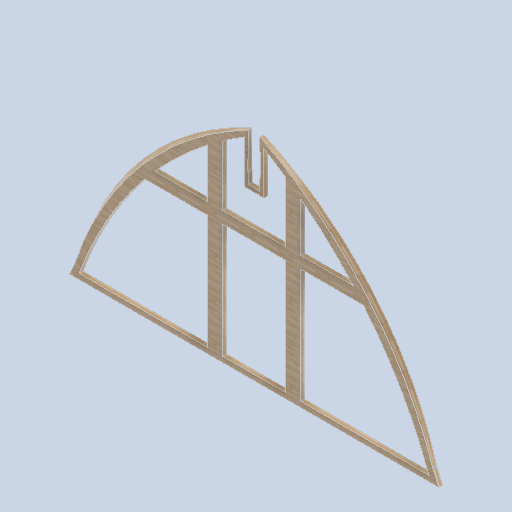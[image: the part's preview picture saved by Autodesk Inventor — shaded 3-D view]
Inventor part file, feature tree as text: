
AUTODESK INVENTOR PART (.ipt)
format: ipt  version: 2024.2 (Build 282272000, 272)  size: 438,784 bytes
history: native  units: mm
features: sketch x4, plane x2, extrude x2, loft x1
ambient origin geometry x8: Origin, YZ Plane, XZ Plane, XY Plane, X Axis, Y Axis, Z Axis, Center Point
bodies: Solid1 (feature_tree)
feature tree (9):
  sketch  "Sketch1"  dims[d2=0.0mm d3=-100.0mm d5=7.0mm]
  plane  "Work Plane2"
  loft  "Loft1"
  extrude  "Extrusion1"  TaperAngle=0.0deg  [1 undecoded]
  extrude  "Extrusion2"  Depth=10000.0mm
  plane  "Work Plane1"
  sketch  "Sketch3"  dims[d6=0.0mm d7=90.0deg d8=0.0mm d9=90.0deg]
  sketch  "Sketch4"  dims[d10=1000.0mm d12=10000.0mm]
  sketch  "Sketch5"  dims[d16=0.0mm d17=0.0mm d20=90.0deg d21=400.0mm d22=90.0deg d23=300.0mm d25=10000.0mm d26=100.0mm d27=0.0mm]
note: 1 required parameter value undecoded (feature->parameter linkage not recoverable at this tier; creation-order binding heuristic only, values carry confidence <= 0.55)
